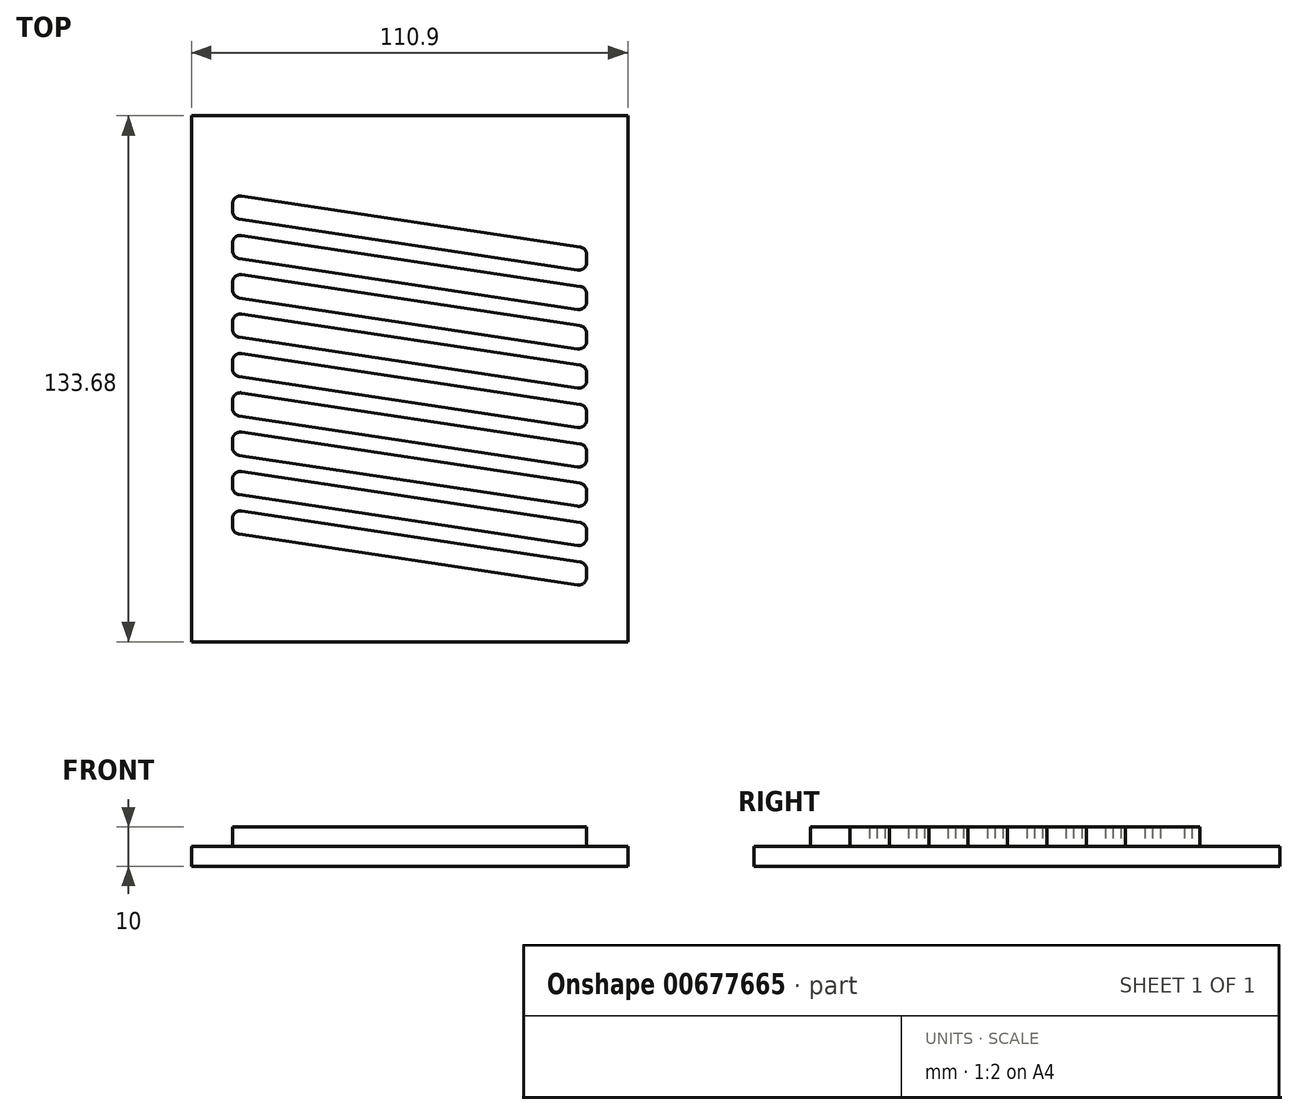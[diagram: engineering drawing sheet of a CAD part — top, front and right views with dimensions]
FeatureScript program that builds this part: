
annotation { "Feature Type Name" : "Feature", "Feature Type Description" : "" }
export const myFeature = defineFeature(function(context is Context, id is Id, definition is map)
    precondition{}
    {
        {
            var Q0;
            Q0=qCreatedBy(makeId("Top.planeOp"),FACE);
            var sketch = newSketch(context, id + "F0", { "sketchPlane" : qUnion([Q0])});
            skLineSegment(sketch, "E0.bottom", {"start": v(-45, -60) * mm, "end": v(45, -60) * mm});
            skLineSegment(sketch, "E0.left", {"start": v(-50, -55) * mm, "end": v(-50, 43.94) * mm});
            skLineSegment(sketch, "E0.right", {"start": v(50, -55) * mm, "end": v(50, 43.82) * mm});
            skPoint(sketch, "E0.middle", {"position": v(0, 0) * mm});
            skLineSegment(sketch, "E1.bottom", {"start": v(-40, -55) * mm, "end": v(10.03, -55) * mm});
            skLineSegment(sketch, "E1.right", {"start": v(45, -55) * mm, "end": v(45, -8.5) * mm, "construction": true});
            skLineSegment(sketch, "E2", {"start": v(-42.7, 6.43) * mm, "end": v(43.3, -6.51) * mm});
            skLineSegment(sketch, "E3", {"start": v(-43.3, 10.56) * mm, "end": v(42.7, -2.38) * mm});
            skLineSegment(sketch, "E4.trimOffspring", {"start": v(-45, 12.5) * mm, "end": v(-45, 12.82) * mm, "construction": true});
            skLineSegment(sketch, "E5.trimOffspring", {"start": v(45, -0.4) * mm, "end": v(45, 289.24) * mm, "construction": true});
            skPoint(sketch, "E6.visualSharp", {"position": v(-44.96, 10.8) * mm});
            skArc(sketch, "E6.filletArc", {"start": v(-45, 12.5) * mm, "mid": v(-44.5, 11.22) * mm, "end": v(-43.3, 10.56) * mm});
            skPoint(sketch, "E7.visualSharp", {"position": v(45, -2.73) * mm});
            skArc(sketch, "E7.filletArc", {"start": v(42.7, -2.38) * mm, "mid": v(44.3, -1.92) * mm, "end": v(45, -0.4) * mm});
            skPoint(sketch, "E8.visualSharp", {"position": v(45, -6.77) * mm});
            skArc(sketch, "E8.filletArc", {"start": v(45, -8.5) * mm, "mid": v(44.5, -7.19) * mm, "end": v(43.3, -6.51) * mm});
            skPoint(sketch, "E9.visualSharp", {"position": v(-45, 6.77) * mm});
            skArc(sketch, "E9.filletArc", {"start": v(-42.7, 6.43) * mm, "mid": v(-44.32, 5.95) * mm, "end": v(-45, 4.4) * mm});
            skLineSegment(sketch, "E10", {"start": v(-45, 1.54) * mm, "end": v(-45, 12.82) * mm, "construction": true});
            skLineSegment(sketch, "E11", {"start": v(45, -13.88) * mm, "end": v(45, 7.22) * mm, "construction": true});
            skLineSegment(sketch, "E12.0.1.0", {"start": v(-42.7, 16.43) * mm, "end": v(43.3, 3.49) * mm});
            skLineSegment(sketch, "E12.0.1.1", {"start": v(-43.3, 20.56) * mm, "end": v(42.7, 7.62) * mm});
            skArc(sketch, "E12.0.1.2", {"start": v(45, 1.5) * mm, "mid": v(44.5, 2.81) * mm, "end": v(43.3, 3.49) * mm});
            skArc(sketch, "E12.0.1.3", {"start": v(42.7, 7.62) * mm, "mid": v(44.3, 8.08) * mm, "end": v(45, 9.6) * mm});
            skArc(sketch, "E12.0.1.4", {"start": v(-42.7, 16.43) * mm, "mid": v(-44.32, 15.95) * mm, "end": v(-45, 14.4) * mm});
            skArc(sketch, "E12.0.1.5", {"start": v(-45, 22.5) * mm, "mid": v(-44.5, 21.22) * mm, "end": v(-43.3, 20.56) * mm});
            skLineSegment(sketch, "E12.0.2.0", {"start": v(-42.7, 26.43) * mm, "end": v(43.3, 13.49) * mm});
            skLineSegment(sketch, "E12.0.2.1", {"start": v(-43.3, 30.56) * mm, "end": v(42.7, 17.62) * mm});
            skArc(sketch, "E12.0.2.2", {"start": v(45, 11.5) * mm, "mid": v(44.5, 12.81) * mm, "end": v(43.3, 13.49) * mm});
            skArc(sketch, "E12.0.2.3", {"start": v(42.7, 17.62) * mm, "mid": v(44.3, 18.08) * mm, "end": v(45, 19.6) * mm});
            skArc(sketch, "E12.0.2.4", {"start": v(-42.7, 26.43) * mm, "mid": v(-44.32, 25.95) * mm, "end": v(-45, 24.4) * mm});
            skArc(sketch, "E12.0.2.5", {"start": v(-45, 32.5) * mm, "mid": v(-44.5, 31.22) * mm, "end": v(-43.3, 30.56) * mm});
            skLineSegment(sketch, "E12.0.3.0", {"start": v(-42.7, 36.43) * mm, "end": v(43.3, 23.49) * mm});
            skLineSegment(sketch, "E12.0.3.1", {"start": v(-43.3, 40.56) * mm, "end": v(42.7, 27.62) * mm});
            skArc(sketch, "E12.0.3.2", {"start": v(45, 21.5) * mm, "mid": v(44.5, 22.81) * mm, "end": v(43.3, 23.49) * mm});
            skArc(sketch, "E12.0.3.3", {"start": v(42.7, 27.62) * mm, "mid": v(44.3, 28.08) * mm, "end": v(45, 29.6) * mm});
            skArc(sketch, "E12.0.3.4", {"start": v(-42.7, 36.43) * mm, "mid": v(-44.32, 35.95) * mm, "end": v(-45, 34.4) * mm});
            skArc(sketch, "E12.0.3.5", {"start": v(-45, 42.5) * mm, "mid": v(-44.5, 41.22) * mm, "end": v(-43.3, 40.56) * mm});
            skLineSegment(sketch, "E12.0.4.0", {"start": v(-42.7, 46.43) * mm, "end": v(43.3, 33.49) * mm});
            skLineSegment(sketch, "E12.0.4.1", {"start": v(-16.92, 46.6) * mm, "end": v(42.7, 37.62) * mm});
            skArc(sketch, "E12.0.4.2", {"start": v(45, 31.5) * mm, "mid": v(44.5, 32.81) * mm, "end": v(43.3, 33.49) * mm});
            skArc(sketch, "E12.0.4.3", {"start": v(42.7, 37.62) * mm, "mid": v(44.3, 38.08) * mm, "end": v(45, 39.6) * mm});
            skArc(sketch, "E12.0.4.4", {"start": v(-42.7, 46.43) * mm, "mid": v(-44.32, 45.95) * mm, "end": v(-45, 44.4) * mm});
            skArc(sketch, "E12.0.5.2", {"start": v(45, 41.5) * mm, "mid": v(44.5, 42.81) * mm, "end": v(43.3, 43.49) * mm});
            skArc(sketch, "E12.0.5.4", {"start": v(-44.92, 55) * mm, "mid": v(-44.99, 54.7) * mm, "end": v(-45, 54.4) * mm});
            skLineSegment(sketch, "E12.1.0.0", {"start": v(-42.71, -3.57) * mm, "end": v(43.28, -16.51) * mm});
            skLineSegment(sketch, "E12.1.0.1", {"start": v(-43.3, 0.56) * mm, "end": v(42.69, -12.38) * mm});
            skArc(sketch, "E12.1.0.2", {"start": v(44.98, -18.5) * mm, "mid": v(44.5, -17.19) * mm, "end": v(43.28, -16.51) * mm});
            skArc(sketch, "E12.1.0.3", {"start": v(42.69, -12.38) * mm, "mid": v(44.29, -11.92) * mm, "end": v(44.98, -10.4) * mm});
            skArc(sketch, "E12.1.0.4", {"start": v(-42.71, -3.57) * mm, "mid": v(-44.33, -4.05) * mm, "end": v(-45.01, -5.6) * mm});
            skArc(sketch, "E12.1.0.5", {"start": v(-45, 2.5) * mm, "mid": v(-44.5, 1.22) * mm, "end": v(-43.3, 0.56) * mm});
            skLineSegment(sketch, "E12.1.1.0", {"start": v(-42.71, 6.43) * mm, "end": v(43.28, -6.51) * mm});
            skLineSegment(sketch, "E12.1.1.1", {"start": v(-43.3, 10.56) * mm, "end": v(42.69, -2.38) * mm});
            skArc(sketch, "E12.1.1.2", {"start": v(44.98, -8.5) * mm, "mid": v(44.5, -7.19) * mm, "end": v(43.28, -6.51) * mm});
            skArc(sketch, "E12.1.1.3", {"start": v(42.69, -2.38) * mm, "mid": v(44.29, -1.92) * mm, "end": v(44.98, -0.4) * mm});
            skArc(sketch, "E12.1.1.4", {"start": v(-42.71, 6.43) * mm, "mid": v(-44.33, 5.95) * mm, "end": v(-45.01, 4.4) * mm});
            skLineSegment(sketch, "E12.1.2.0", {"start": v(-42.71, 16.43) * mm, "end": v(43.28, 3.49) * mm});
            skLineSegment(sketch, "E12.1.2.1", {"start": v(-43.3, 20.56) * mm, "end": v(42.69, 7.62) * mm});
            skArc(sketch, "E12.1.2.2", {"start": v(44.98, 1.5) * mm, "mid": v(44.5, 2.81) * mm, "end": v(43.28, 3.49) * mm});
            skArc(sketch, "E12.1.2.3", {"start": v(42.69, 7.62) * mm, "mid": v(44.29, 8.08) * mm, "end": v(44.98, 9.6) * mm});
            skArc(sketch, "E12.1.2.4", {"start": v(-42.71, 16.43) * mm, "mid": v(-44.33, 15.95) * mm, "end": v(-45.01, 14.4) * mm});
            skArc(sketch, "E12.1.2.5", {"start": v(-45, 22.5) * mm, "mid": v(-44.5, 21.22) * mm, "end": v(-43.3, 20.56) * mm});
            skLineSegment(sketch, "E12.1.3.0", {"start": v(-42.71, 26.43) * mm, "end": v(43.28, 13.49) * mm});
            skLineSegment(sketch, "E12.1.3.1", {"start": v(-43.3, 30.56) * mm, "end": v(42.69, 17.62) * mm});
            skArc(sketch, "E12.1.3.2", {"start": v(44.98, 11.5) * mm, "mid": v(44.5, 12.81) * mm, "end": v(43.28, 13.49) * mm});
            skArc(sketch, "E12.1.3.3", {"start": v(42.69, 17.62) * mm, "mid": v(44.29, 18.08) * mm, "end": v(44.98, 19.6) * mm});
            skArc(sketch, "E12.1.3.4", {"start": v(-42.71, 26.43) * mm, "mid": v(-44.33, 25.95) * mm, "end": v(-45.01, 24.4) * mm});
            skArc(sketch, "E12.1.3.5", {"start": v(-45, 32.5) * mm, "mid": v(-44.5, 31.22) * mm, "end": v(-43.3, 30.56) * mm});
            skLineSegment(sketch, "E12.1.4.0", {"start": v(-42.71, 36.43) * mm, "end": v(43.28, 23.49) * mm});
            skLineSegment(sketch, "E12.1.4.1", {"start": v(-43.3, 40.56) * mm, "end": v(42.69, 27.62) * mm});
            skArc(sketch, "E12.1.4.2", {"start": v(44.98, 21.5) * mm, "mid": v(44.5, 22.81) * mm, "end": v(43.28, 23.49) * mm});
            skArc(sketch, "E12.1.4.3", {"start": v(42.69, 27.62) * mm, "mid": v(44.29, 28.08) * mm, "end": v(44.98, 29.6) * mm});
            skArc(sketch, "E12.1.4.4", {"start": v(-42.71, 36.43) * mm, "mid": v(-44.33, 35.95) * mm, "end": v(-45.01, 34.4) * mm});
            skArc(sketch, "E12.1.4.5", {"start": v(-45, 42.5) * mm, "mid": v(-44.5, 41.22) * mm, "end": v(-43.3, 40.56) * mm});
            skLineSegment(sketch, "E12.1.5.0", {"start": v(-42.71, 46.43) * mm, "end": v(43.28, 33.49) * mm});
            skArc(sketch, "E12.1.5.2", {"start": v(44.98, 31.5) * mm, "mid": v(44.5, 32.81) * mm, "end": v(43.28, 33.49) * mm});
            skArc(sketch, "E12.1.5.3", {"start": v(42.69, 37.62) * mm, "mid": v(44.29, 38.08) * mm, "end": v(44.98, 39.6) * mm});
            skArc(sketch, "E12.1.5.4", {"start": v(-42.71, 46.43) * mm, "mid": v(-44.33, 45.95) * mm, "end": v(-45.01, 44.4) * mm});
            skLineSegment(sketch, "E12.2.0.0", {"start": v(-42.72, -13.57) * mm, "end": v(43.27, -26.51) * mm});
            skLineSegment(sketch, "E12.2.0.1", {"start": v(-43.31, -9.44) * mm, "end": v(42.68, -22.38) * mm});
            skArc(sketch, "E12.2.0.2", {"start": v(44.97, -28.5) * mm, "mid": v(44.49, -27.19) * mm, "end": v(43.27, -26.51) * mm});
            skArc(sketch, "E12.2.0.3", {"start": v(42.68, -22.38) * mm, "mid": v(44.28, -21.92) * mm, "end": v(44.97, -20.4) * mm});
            skArc(sketch, "E12.2.0.4", {"start": v(-42.72, -13.57) * mm, "mid": v(-44.34, -14.05) * mm, "end": v(-45.02, -15.6) * mm});
            skArc(sketch, "E12.2.0.5", {"start": v(-45.01, -7.5) * mm, "mid": v(-44.51, -8.78) * mm, "end": v(-43.31, -9.44) * mm});
            skLineSegment(sketch, "E12.2.1.0", {"start": v(-42.72, -3.57) * mm, "end": v(43.27, -16.51) * mm});
            skLineSegment(sketch, "E12.2.1.1", {"start": v(-43.31, 0.56) * mm, "end": v(42.68, -12.38) * mm});
            skArc(sketch, "E12.2.1.2", {"start": v(44.97, -18.5) * mm, "mid": v(44.49, -17.19) * mm, "end": v(43.27, -16.51) * mm});
            skArc(sketch, "E12.2.1.3", {"start": v(42.68, -12.38) * mm, "mid": v(44.28, -11.92) * mm, "end": v(44.97, -10.4) * mm});
            skArc(sketch, "E12.2.1.4", {"start": v(-42.72, -3.57) * mm, "mid": v(-44.34, -4.05) * mm, "end": v(-45.02, -5.6) * mm});
            skArc(sketch, "E12.2.1.5", {"start": v(-45.01, 2.5) * mm, "mid": v(-44.51, 1.22) * mm, "end": v(-43.31, 0.56) * mm});
            skLineSegment(sketch, "E12.2.2.0", {"start": v(-42.72, 6.43) * mm, "end": v(43.27, -6.51) * mm});
            skLineSegment(sketch, "E12.2.2.1", {"start": v(-43.31, 10.56) * mm, "end": v(42.68, -2.38) * mm});
            skArc(sketch, "E12.2.2.2", {"start": v(44.97, -8.5) * mm, "mid": v(44.49, -7.19) * mm, "end": v(43.27, -6.51) * mm});
            skArc(sketch, "E12.2.2.3", {"start": v(42.68, -2.38) * mm, "mid": v(44.28, -1.92) * mm, "end": v(44.97, -0.4) * mm});
            skArc(sketch, "E12.2.2.4", {"start": v(-42.72, 6.43) * mm, "mid": v(-44.34, 5.95) * mm, "end": v(-45.02, 4.4) * mm});
            skArc(sketch, "E12.2.2.5", {"start": v(-45.01, 12.5) * mm, "mid": v(-44.51, 11.22) * mm, "end": v(-43.31, 10.56) * mm});
            skLineSegment(sketch, "E12.2.3.0", {"start": v(-42.72, 16.43) * mm, "end": v(43.27, 3.49) * mm});
            skLineSegment(sketch, "E12.2.3.1", {"start": v(-43.31, 20.56) * mm, "end": v(42.68, 7.62) * mm});
            skArc(sketch, "E12.2.3.2", {"start": v(44.97, 1.5) * mm, "mid": v(44.49, 2.81) * mm, "end": v(43.27, 3.49) * mm});
            skArc(sketch, "E12.2.3.3", {"start": v(42.68, 7.62) * mm, "mid": v(44.28, 8.08) * mm, "end": v(44.97, 9.6) * mm});
            skArc(sketch, "E12.2.3.4", {"start": v(-42.72, 16.43) * mm, "mid": v(-44.34, 15.95) * mm, "end": v(-45.02, 14.4) * mm});
            skArc(sketch, "E12.2.3.5", {"start": v(-45.01, 22.5) * mm, "mid": v(-44.51, 21.22) * mm, "end": v(-43.31, 20.56) * mm});
            skLineSegment(sketch, "E12.2.4.0", {"start": v(-42.72, 26.43) * mm, "end": v(43.27, 13.49) * mm});
            skLineSegment(sketch, "E12.2.4.1", {"start": v(-43.31, 30.56) * mm, "end": v(42.68, 17.62) * mm});
            skArc(sketch, "E12.2.4.2", {"start": v(44.97, 11.5) * mm, "mid": v(44.49, 12.81) * mm, "end": v(43.27, 13.49) * mm});
            skArc(sketch, "E12.2.4.3", {"start": v(42.68, 17.62) * mm, "mid": v(44.28, 18.08) * mm, "end": v(44.97, 19.6) * mm});
            skArc(sketch, "E12.2.4.4", {"start": v(-42.72, 26.43) * mm, "mid": v(-44.34, 25.95) * mm, "end": v(-45.02, 24.4) * mm});
            skArc(sketch, "E12.2.4.5", {"start": v(-45.01, 32.5) * mm, "mid": v(-44.51, 31.22) * mm, "end": v(-43.31, 30.56) * mm});
            skLineSegment(sketch, "E12.2.5.0", {"start": v(-42.72, 36.43) * mm, "end": v(43.27, 23.49) * mm});
            skLineSegment(sketch, "E12.2.5.1", {"start": v(-43.31, 40.56) * mm, "end": v(42.68, 27.62) * mm});
            skArc(sketch, "E12.2.5.2", {"start": v(44.97, 21.5) * mm, "mid": v(44.49, 22.81) * mm, "end": v(43.27, 23.49) * mm});
            skArc(sketch, "E12.2.5.3", {"start": v(42.68, 27.62) * mm, "mid": v(44.28, 28.08) * mm, "end": v(44.97, 29.6) * mm});
            skArc(sketch, "E12.2.5.4", {"start": v(-42.72, 36.43) * mm, "mid": v(-44.34, 35.95) * mm, "end": v(-45.02, 34.4) * mm});
            skArc(sketch, "E12.2.5.5", {"start": v(-45.01, 42.5) * mm, "mid": v(-44.51, 41.22) * mm, "end": v(-43.31, 40.56) * mm});
            skLineSegment(sketch, "E12.3.0.0", {"start": v(-42.73, -23.57) * mm, "end": v(43.26, -36.51) * mm});
            skLineSegment(sketch, "E12.3.0.1", {"start": v(-43.32, -19.44) * mm, "end": v(42.67, -32.38) * mm});
            skArc(sketch, "E12.3.0.2", {"start": v(44.96, -38.5) * mm, "mid": v(44.48, -37.19) * mm, "end": v(43.26, -36.51) * mm});
            skArc(sketch, "E12.3.0.3", {"start": v(42.67, -32.38) * mm, "mid": v(44.27, -31.92) * mm, "end": v(44.96, -30.4) * mm});
            skArc(sketch, "E12.3.0.4", {"start": v(-42.73, -23.57) * mm, "mid": v(-44.35, -24.05) * mm, "end": v(-45.03, -25.6) * mm});
            skArc(sketch, "E12.3.0.5", {"start": v(-45.02, -17.5) * mm, "mid": v(-44.52, -18.78) * mm, "end": v(-43.32, -19.44) * mm});
            skLineSegment(sketch, "E12.3.1.0", {"start": v(-42.73, -13.57) * mm, "end": v(43.26, -26.51) * mm});
            skLineSegment(sketch, "E12.3.1.1", {"start": v(-43.32, -9.44) * mm, "end": v(42.67, -22.38) * mm});
            skArc(sketch, "E12.3.1.2", {"start": v(44.96, -28.5) * mm, "mid": v(44.48, -27.19) * mm, "end": v(43.26, -26.51) * mm});
            skArc(sketch, "E12.3.1.3", {"start": v(42.67, -22.38) * mm, "mid": v(44.27, -21.92) * mm, "end": v(44.96, -20.4) * mm});
            skArc(sketch, "E12.3.1.4", {"start": v(-42.73, -13.57) * mm, "mid": v(-44.35, -14.05) * mm, "end": v(-45.03, -15.6) * mm});
            skArc(sketch, "E12.3.1.5", {"start": v(-45.02, -7.5) * mm, "mid": v(-44.52, -8.78) * mm, "end": v(-43.32, -9.44) * mm});
            skLineSegment(sketch, "E12.3.2.0", {"start": v(-42.73, -3.57) * mm, "end": v(43.26, -16.51) * mm});
            skLineSegment(sketch, "E12.3.2.1", {"start": v(-43.32, 0.56) * mm, "end": v(42.67, -12.38) * mm});
            skArc(sketch, "E12.3.2.2", {"start": v(44.96, -18.5) * mm, "mid": v(44.48, -17.19) * mm, "end": v(43.26, -16.51) * mm});
            skArc(sketch, "E12.3.2.3", {"start": v(42.67, -12.38) * mm, "mid": v(44.27, -11.92) * mm, "end": v(44.96, -10.4) * mm});
            skArc(sketch, "E12.3.2.4", {"start": v(-42.73, -3.57) * mm, "mid": v(-44.35, -4.05) * mm, "end": v(-45.03, -5.6) * mm});
            skArc(sketch, "E12.3.2.5", {"start": v(-45.02, 2.5) * mm, "mid": v(-44.52, 1.22) * mm, "end": v(-43.32, 0.56) * mm});
            skLineSegment(sketch, "E12.3.3.0", {"start": v(-42.73, 6.43) * mm, "end": v(43.26, -6.51) * mm});
            skLineSegment(sketch, "E12.3.3.1", {"start": v(-43.32, 10.56) * mm, "end": v(42.67, -2.38) * mm});
            skArc(sketch, "E12.3.3.2", {"start": v(44.96, -8.5) * mm, "mid": v(44.48, -7.19) * mm, "end": v(43.26, -6.51) * mm});
            skArc(sketch, "E12.3.3.3", {"start": v(42.67, -2.38) * mm, "mid": v(44.27, -1.92) * mm, "end": v(44.96, -0.4) * mm});
            skArc(sketch, "E12.3.3.4", {"start": v(-42.73, 6.43) * mm, "mid": v(-44.35, 5.95) * mm, "end": v(-45.03, 4.4) * mm});
            skArc(sketch, "E12.3.3.5", {"start": v(-45.02, 12.5) * mm, "mid": v(-44.52, 11.22) * mm, "end": v(-43.32, 10.56) * mm});
            skLineSegment(sketch, "E12.3.4.0", {"start": v(-42.73, 16.43) * mm, "end": v(43.26, 3.49) * mm});
            skLineSegment(sketch, "E12.3.4.1", {"start": v(-43.32, 20.56) * mm, "end": v(42.67, 7.62) * mm});
            skArc(sketch, "E12.3.4.2", {"start": v(44.96, 1.5) * mm, "mid": v(44.48, 2.81) * mm, "end": v(43.26, 3.49) * mm});
            skArc(sketch, "E12.3.4.3", {"start": v(42.67, 7.62) * mm, "mid": v(44.27, 8.08) * mm, "end": v(44.96, 9.6) * mm});
            skArc(sketch, "E12.3.4.4", {"start": v(-42.73, 16.43) * mm, "mid": v(-44.35, 15.95) * mm, "end": v(-45.03, 14.4) * mm});
            skArc(sketch, "E12.3.4.5", {"start": v(-45.02, 22.5) * mm, "mid": v(-44.52, 21.22) * mm, "end": v(-43.32, 20.56) * mm});
            skLineSegment(sketch, "E12.3.5.0", {"start": v(-42.73, 26.43) * mm, "end": v(43.26, 13.49) * mm});
            skLineSegment(sketch, "E12.3.5.1", {"start": v(-43.32, 30.56) * mm, "end": v(42.67, 17.62) * mm});
            skArc(sketch, "E12.3.5.2", {"start": v(44.96, 11.5) * mm, "mid": v(44.48, 12.81) * mm, "end": v(43.26, 13.49) * mm});
            skArc(sketch, "E12.3.5.3", {"start": v(42.67, 17.62) * mm, "mid": v(44.27, 18.08) * mm, "end": v(44.96, 19.6) * mm});
            skArc(sketch, "E12.3.5.4", {"start": v(-42.73, 26.43) * mm, "mid": v(-44.35, 25.95) * mm, "end": v(-45.03, 24.4) * mm});
            skArc(sketch, "E12.3.5.5", {"start": v(-45.02, 32.5) * mm, "mid": v(-44.52, 31.22) * mm, "end": v(-43.32, 30.56) * mm});
            skLineSegment(sketch, "E12.4.0.0", {"start": v(-42.74, -33.57) * mm, "end": v(43.25, -46.51) * mm});
            skLineSegment(sketch, "E12.4.0.1", {"start": v(-43.33, -29.44) * mm, "end": v(42.66, -42.38) * mm});
            skArc(sketch, "E12.4.0.2", {"start": v(44.95, -48.5) * mm, "mid": v(44.47, -47.19) * mm, "end": v(43.25, -46.51) * mm});
            skArc(sketch, "E12.4.0.3", {"start": v(42.66, -42.38) * mm, "mid": v(44.26, -41.92) * mm, "end": v(44.95, -40.4) * mm});
            skArc(sketch, "E12.4.0.4", {"start": v(-42.74, -33.57) * mm, "mid": v(-44.36, -34.05) * mm, "end": v(-45.04, -35.6) * mm});
            skArc(sketch, "E12.4.0.5", {"start": v(-45.03, -27.5) * mm, "mid": v(-44.53, -28.78) * mm, "end": v(-43.33, -29.44) * mm});
            skLineSegment(sketch, "E12.4.1.0", {"start": v(-42.74, -23.57) * mm, "end": v(43.25, -36.51) * mm});
            skLineSegment(sketch, "E12.4.1.1", {"start": v(-43.33, -19.44) * mm, "end": v(42.66, -32.38) * mm});
            skArc(sketch, "E12.4.1.2", {"start": v(44.95, -38.5) * mm, "mid": v(44.47, -37.19) * mm, "end": v(43.25, -36.51) * mm});
            skArc(sketch, "E12.4.1.3", {"start": v(42.66, -32.38) * mm, "mid": v(44.26, -31.92) * mm, "end": v(44.95, -30.4) * mm});
            skArc(sketch, "E12.4.1.4", {"start": v(-42.74, -23.57) * mm, "mid": v(-44.36, -24.05) * mm, "end": v(-45.04, -25.6) * mm});
            skArc(sketch, "E12.4.1.5", {"start": v(-45.03, -17.5) * mm, "mid": v(-44.53, -18.78) * mm, "end": v(-43.33, -19.44) * mm});
            skLineSegment(sketch, "E12.4.2.0", {"start": v(-42.74, -13.57) * mm, "end": v(43.25, -26.51) * mm});
            skLineSegment(sketch, "E12.4.2.1", {"start": v(-43.33, -9.44) * mm, "end": v(42.66, -22.38) * mm});
            skArc(sketch, "E12.4.2.2", {"start": v(44.95, -28.5) * mm, "mid": v(44.47, -27.19) * mm, "end": v(43.25, -26.51) * mm});
            skArc(sketch, "E12.4.2.3", {"start": v(42.66, -22.38) * mm, "mid": v(44.26, -21.92) * mm, "end": v(44.95, -20.4) * mm});
            skArc(sketch, "E12.4.2.4", {"start": v(-42.74, -13.57) * mm, "mid": v(-44.36, -14.05) * mm, "end": v(-45.04, -15.6) * mm});
            skArc(sketch, "E12.4.2.5", {"start": v(-45.03, -7.5) * mm, "mid": v(-44.53, -8.78) * mm, "end": v(-43.33, -9.44) * mm});
            skLineSegment(sketch, "E12.4.3.0", {"start": v(-42.74, -3.57) * mm, "end": v(43.25, -16.51) * mm});
            skLineSegment(sketch, "E12.4.3.1", {"start": v(-43.33, 0.56) * mm, "end": v(42.66, -12.38) * mm});
            skArc(sketch, "E12.4.3.2", {"start": v(44.95, -18.5) * mm, "mid": v(44.47, -17.19) * mm, "end": v(43.25, -16.51) * mm});
            skArc(sketch, "E12.4.3.3", {"start": v(42.66, -12.38) * mm, "mid": v(44.26, -11.92) * mm, "end": v(44.95, -10.4) * mm});
            skArc(sketch, "E12.4.3.4", {"start": v(-42.74, -3.57) * mm, "mid": v(-44.36, -4.05) * mm, "end": v(-45.04, -5.6) * mm});
            skArc(sketch, "E12.4.3.5", {"start": v(-45.03, 2.5) * mm, "mid": v(-44.53, 1.22) * mm, "end": v(-43.33, 0.56) * mm});
            skLineSegment(sketch, "E12.4.4.0", {"start": v(-42.74, 6.43) * mm, "end": v(43.25, -6.51) * mm});
            skLineSegment(sketch, "E12.4.4.1", {"start": v(-43.33, 10.56) * mm, "end": v(42.66, -2.38) * mm});
            skArc(sketch, "E12.4.4.2", {"start": v(44.95, -8.5) * mm, "mid": v(44.47, -7.19) * mm, "end": v(43.25, -6.51) * mm});
            skArc(sketch, "E12.4.4.3", {"start": v(42.66, -2.38) * mm, "mid": v(44.26, -1.92) * mm, "end": v(44.95, -0.4) * mm});
            skArc(sketch, "E12.4.4.4", {"start": v(-42.74, 6.43) * mm, "mid": v(-44.36, 5.95) * mm, "end": v(-45.04, 4.4) * mm});
            skArc(sketch, "E12.4.4.5", {"start": v(-45.03, 12.5) * mm, "mid": v(-44.53, 11.22) * mm, "end": v(-43.33, 10.56) * mm});
            skLineSegment(sketch, "E12.4.5.0", {"start": v(-42.74, 16.43) * mm, "end": v(43.25, 3.49) * mm});
            skLineSegment(sketch, "E12.4.5.1", {"start": v(-43.33, 20.56) * mm, "end": v(42.66, 7.62) * mm});
            skArc(sketch, "E12.4.5.2", {"start": v(44.95, 1.5) * mm, "mid": v(44.47, 2.81) * mm, "end": v(43.25, 3.49) * mm});
            skArc(sketch, "E12.4.5.3", {"start": v(42.66, 7.62) * mm, "mid": v(44.26, 8.08) * mm, "end": v(44.95, 9.6) * mm});
            skArc(sketch, "E12.4.5.4", {"start": v(-42.74, 16.43) * mm, "mid": v(-44.36, 15.95) * mm, "end": v(-45.04, 14.4) * mm});
            skArc(sketch, "E12.4.5.5", {"start": v(-45.03, 22.5) * mm, "mid": v(-44.53, 21.22) * mm, "end": v(-43.33, 20.56) * mm});
            skLineSegment(sketch, "E12.5.0.0", {"start": v(-42.75, -43.57) * mm, "end": v(-7.57, -48.87) * mm});
            skLineSegment(sketch, "E12.5.0.1", {"start": v(-43.34, -39.44) * mm, "end": v(42.65, -52.38) * mm});
            skArc(sketch, "E12.5.0.3", {"start": v(42.65, -52.38) * mm, "mid": v(44.25, -51.92) * mm, "end": v(44.94, -50.4) * mm});
            skArc(sketch, "E12.5.0.4", {"start": v(-42.75, -43.57) * mm, "mid": v(-44.37, -44.05) * mm, "end": v(-45.05, -45.6) * mm});
            skArc(sketch, "E12.5.0.5", {"start": v(-45.04, -37.5) * mm, "mid": v(-44.54, -38.78) * mm, "end": v(-43.34, -39.44) * mm});
            skLineSegment(sketch, "E12.5.1.0", {"start": v(-42.75, -33.57) * mm, "end": v(43.24, -46.51) * mm});
            skLineSegment(sketch, "E12.5.1.1", {"start": v(-43.34, -29.44) * mm, "end": v(42.65, -42.38) * mm});
            skArc(sketch, "E12.5.1.2", {"start": v(44.94, -48.5) * mm, "mid": v(44.46, -47.19) * mm, "end": v(43.24, -46.51) * mm});
            skArc(sketch, "E12.5.1.3", {"start": v(42.65, -42.38) * mm, "mid": v(44.25, -41.92) * mm, "end": v(44.94, -40.4) * mm});
            skArc(sketch, "E12.5.1.4", {"start": v(-42.75, -33.57) * mm, "mid": v(-44.37, -34.05) * mm, "end": v(-45.05, -35.6) * mm});
            skArc(sketch, "E12.5.1.5", {"start": v(-45.04, -27.5) * mm, "mid": v(-44.54, -28.78) * mm, "end": v(-43.34, -29.44) * mm});
            skLineSegment(sketch, "E12.5.2.0", {"start": v(-42.75, -23.57) * mm, "end": v(43.24, -36.51) * mm});
            skLineSegment(sketch, "E12.5.2.1", {"start": v(-43.34, -19.44) * mm, "end": v(42.65, -32.38) * mm});
            skArc(sketch, "E12.5.2.2", {"start": v(44.94, -38.5) * mm, "mid": v(44.46, -37.19) * mm, "end": v(43.24, -36.51) * mm});
            skArc(sketch, "E12.5.2.3", {"start": v(42.65, -32.38) * mm, "mid": v(44.25, -31.92) * mm, "end": v(44.94, -30.4) * mm});
            skArc(sketch, "E12.5.2.4", {"start": v(-42.75, -23.57) * mm, "mid": v(-44.37, -24.05) * mm, "end": v(-45.05, -25.6) * mm});
            skArc(sketch, "E12.5.2.5", {"start": v(-45.04, -17.5) * mm, "mid": v(-44.54, -18.78) * mm, "end": v(-43.34, -19.44) * mm});
            skLineSegment(sketch, "E12.5.3.0", {"start": v(-42.75, -13.57) * mm, "end": v(43.24, -26.51) * mm});
            skLineSegment(sketch, "E12.5.3.1", {"start": v(-43.34, -9.44) * mm, "end": v(42.65, -22.38) * mm});
            skArc(sketch, "E12.5.3.2", {"start": v(44.94, -28.5) * mm, "mid": v(44.46, -27.19) * mm, "end": v(43.24, -26.51) * mm});
            skArc(sketch, "E12.5.3.3", {"start": v(42.65, -22.38) * mm, "mid": v(44.25, -21.92) * mm, "end": v(44.94, -20.4) * mm});
            skArc(sketch, "E12.5.3.4", {"start": v(-42.75, -13.57) * mm, "mid": v(-44.37, -14.05) * mm, "end": v(-45.05, -15.6) * mm});
            skArc(sketch, "E12.5.3.5", {"start": v(-45.04, -7.5) * mm, "mid": v(-44.54, -8.78) * mm, "end": v(-43.34, -9.44) * mm});
            skLineSegment(sketch, "E12.5.4.0", {"start": v(-42.75, -3.57) * mm, "end": v(43.24, -16.51) * mm});
            skLineSegment(sketch, "E12.5.4.1", {"start": v(-43.34, 0.56) * mm, "end": v(42.65, -12.38) * mm});
            skArc(sketch, "E12.5.4.2", {"start": v(44.94, -18.5) * mm, "mid": v(44.46, -17.19) * mm, "end": v(43.24, -16.51) * mm});
            skArc(sketch, "E12.5.4.3", {"start": v(42.65, -12.38) * mm, "mid": v(44.25, -11.92) * mm, "end": v(44.94, -10.4) * mm});
            skArc(sketch, "E12.5.4.4", {"start": v(-42.75, -3.57) * mm, "mid": v(-44.37, -4.05) * mm, "end": v(-45.05, -5.6) * mm});
            skArc(sketch, "E12.5.4.5", {"start": v(-45.04, 2.5) * mm, "mid": v(-44.54, 1.22) * mm, "end": v(-43.34, 0.56) * mm});
            skLineSegment(sketch, "E12.5.5.0", {"start": v(-42.75, 6.43) * mm, "end": v(43.24, -6.51) * mm});
            skLineSegment(sketch, "E12.5.5.1", {"start": v(-43.34, 10.56) * mm, "end": v(42.65, -2.38) * mm});
            skArc(sketch, "E12.5.5.2", {"start": v(44.94, -8.5) * mm, "mid": v(44.46, -7.19) * mm, "end": v(43.24, -6.51) * mm});
            skArc(sketch, "E12.5.5.3", {"start": v(42.65, -2.38) * mm, "mid": v(44.25, -1.92) * mm, "end": v(44.94, -0.4) * mm});
            skArc(sketch, "E12.5.5.4", {"start": v(-42.75, 6.43) * mm, "mid": v(-44.37, 5.95) * mm, "end": v(-45.05, 4.4) * mm});
            skArc(sketch, "E12.5.5.5", {"start": v(-45.04, 12.5) * mm, "mid": v(-44.54, 11.22) * mm, "end": v(-43.34, 10.56) * mm});
            skLineSegment(sketch, "E12.direction1", {"start": v(-42.7, 6.43) * mm, "end": v(-42.71, -3.57) * mm, "construction": true});
            skLineSegment(sketch, "E12.direction2", {"start": v(-42.7, 6.43) * mm, "end": v(-42.7, 16.43) * mm, "construction": true});
            skPoint(sketch, "E13.orphan", {"position": v(-42.7, 56.43) * mm});
            skPoint(sketch, "E14.visualSharp", {"position": v(45, 55) * mm});
            skPoint(sketch, "E15.visualSharp", {"position": v(50, 60) * mm});
            skPoint(sketch, "E16.visualSharp", {"position": v(-50, 60) * mm});
            skPoint(sketch, "E17.visualSharp", {"position": v(50, -60) * mm});
            skArc(sketch, "E17.filletArc", {"start": v(45, -60) * mm, "mid": v(48.54, -58.54) * mm, "end": v(50, -55) * mm});
            skPoint(sketch, "E18.visualSharp", {"position": v(-45, -55) * mm});
            skArc(sketch, "E18.filletArc", {"start": v(-45, -50) * mm, "mid": v(-43.54, -53.54) * mm, "end": v(-40, -55) * mm});
            skPoint(sketch, "E19.visualSharp", {"position": v(-50, -60) * mm});
            skArc(sketch, "E19.filletArc", {"start": v(-50, -55) * mm, "mid": v(-48.54, -58.54) * mm, "end": v(-45, -60) * mm});
            skLineSegment(sketch, "E20", {"start": v(-6.98, 65.52) * mm, "end": v(-5, 65.52) * mm});
            skLineSegment(sketch, "E21", {"start": v(-5, 65.52) * mm, "end": v(-5, 62.51) * mm});
            skLineSegment(sketch, "E22", {"start": v(-5, 62.51) * mm, "end": v(5, 62.51) * mm});
            skLineSegment(sketch, "E23", {"start": v(5, 62.51) * mm, "end": v(5, 65.52) * mm});
            skLineSegment(sketch, "E24", {"start": v(-43.5, 51.8) * mm, "end": v(-16.56, 56.91) * mm});
            skLineSegment(sketch, "E25", {"start": v(43.4, 51.7) * mm, "end": v(18.5, 56.14) * mm});
            skArc(sketch, "E26.trimOffspring", {"start": v(-43.3, 50.52) * mm, "mid": v(-43.3, 50.54) * mm, "end": v(-43.3, 50.56) * mm});
            skPoint(sketch, "E27.orphan", {"position": v(-45, 52.5) * mm});
            skLineSegment(sketch, "E28.trimOffspring", {"start": v(-16.04, 52.41) * mm, "end": v(43.3, 43.49) * mm});
            skPoint(sketch, "E29.endSnap0", {"position": v(44.5, 42.81) * mm});
            skPoint(sketch, "E30.visualSharp", {"position": v(-18.02, 52.71) * mm});
            skLineSegment(sketch, "E31", {"start": v(-18.32, 50.73) * mm, "end": v(-18.6, 48.87) * mm});
            skArc(sketch, "E32.filletArc", {"start": v(-16.04, 52.41) * mm, "mid": v(-17.53, 52.04) * mm, "end": v(-18.32, 50.73) * mm});
            skPoint(sketch, "E33.newPointB", {"position": v(-43.3, 50.56) * mm});
            skArc(sketch, "E33.filletArc", {"start": v(-18.6, 48.87) * mm, "mid": v(-18.23, 47.38) * mm, "end": v(-16.92, 46.6) * mm});
            skLineSegment(sketch, "E34.trimOffspring", {"start": v(5, 65.52) * mm, "end": v(6.98, 65.52) * mm});
            skLineSegment(sketch, "E35", {"start": v(-13, 60.9) * mm, "end": v(-13, 65.52) * mm});
            skLineSegment(sketch, "E36", {"start": v(-13, 65.52) * mm, "end": v(-6.98, 65.52) * mm});
            skLineSegment(sketch, "E37", {"start": v(13, 61.09) * mm, "end": v(13, 65.52) * mm});
            skLineSegment(sketch, "E38", {"start": v(13, 65.52) * mm, "end": v(6.98, 65.52) * mm});
            skPoint(sketch, "E39.visualSharp", {"position": v(-13, 57.59) * mm});
            skPoint(sketch, "E40.visualSharp", {"position": v(13, 57.12) * mm});
            skLineSegment(sketch, "E41", {"start": v(-5, 65.52) * mm, "end": v(-5, 58.52) * mm});
            skPoint(sketch, "E42.visualSharp", {"position": v(-50, 50.56) * mm});
            skArc(sketch, "E42.filletArc", {"start": v(-43.5, 51.8) * mm, "mid": v(-48.16, 49.04) * mm, "end": v(-50, 43.94) * mm});
            skPoint(sketch, "E43.visualSharp", {"position": v(50, 50.51) * mm});
            skArc(sketch, "E43.filletArc", {"start": v(50, 43.82) * mm, "mid": v(48.13, 48.95) * mm, "end": v(43.4, 51.7) * mm});
            skLineSegment(sketch, "E44", {"start": v(-45, 44.4) * mm, "end": v(-45, 42.5) * mm});
            skLineSegment(sketch, "E45", {"start": v(-45, 34.4) * mm, "end": v(-45, 32.5) * mm});
            skLineSegment(sketch, "E46", {"start": v(-45, 24.4) * mm, "end": v(-45, 22.5) * mm});
            skLineSegment(sketch, "E47", {"start": v(-45, 14.4) * mm, "end": v(-45, 12.5) * mm});
            skLineSegment(sketch, "E48", {"start": v(-45, 4.4) * mm, "end": v(-45, 2.5) * mm});
            skLineSegment(sketch, "E49", {"start": v(-45.02, -15.6) * mm, "end": v(-45.02, -17.5) * mm});
            skLineSegment(sketch, "E50", {"start": v(-45.03, -25.6) * mm, "end": v(-45.03, -27.5) * mm});
            skLineSegment(sketch, "E51", {"start": v(-45.04, -35.6) * mm, "end": v(-45.04, -37.5) * mm});
            skLineSegment(sketch, "E52", {"start": v(44.94, -50.4) * mm, "end": v(44.95, -48.5) * mm});
            skLineSegment(sketch, "E53", {"start": v(44.95, -40.4) * mm, "end": v(44.96, -38.5) * mm});
            skLineSegment(sketch, "E54", {"start": v(44.96, -30.4) * mm, "end": v(44.97, -28.5) * mm});
            skLineSegment(sketch, "E55", {"start": v(45, -0.4) * mm, "end": v(45, 1.5) * mm});
            skLineSegment(sketch, "E56", {"start": v(44.98, -10.4) * mm, "end": v(45, -8.5) * mm});
            skLineSegment(sketch, "E57", {"start": v(45, 11.5) * mm, "end": v(45, 9.6) * mm});
            skLineSegment(sketch, "E58", {"start": v(45, 19.6) * mm, "end": v(45, 21.5) * mm});
            skLineSegment(sketch, "E59", {"start": v(45, 29.6) * mm, "end": v(45, 31.5) * mm});
            skLineSegment(sketch, "E60", {"start": v(45, 39.6) * mm, "end": v(45, 41.5) * mm});
            skLineSegment(sketch, "E61", {"start": v(-45, -49.24) * mm, "end": v(-45.05, -45.6) * mm});
            skLineSegment(sketch, "E62", {"start": v(-45, -50) * mm, "end": v(-45, -49.24) * mm});
            skPoint(sketch, "E63.newPointB", {"position": v(-5.6, -49.24) * mm});
            skPoint(sketch, "E64.visualSharp", {"position": v(-6.46, -55) * mm});
            skLineSegment(sketch, "E65", {"start": v(-45.01, -5.6) * mm, "end": v(-45.01, -7.5) * mm});
            skLineSegment(sketch, "E66", {"start": v(44.98, -18.5) * mm, "end": v(44.97, -20.4) * mm});
            skLineSegment(sketch, "E67", {"start": v(-7.57, -48.87) * mm, "end": v(10.17, -51.54) * mm});
            skLineSegment(sketch, "E68", {"start": v(11.03, -52.53) * mm, "end": v(11.03, -54) * mm});
            skPoint(sketch, "E69.visualSharp", {"position": v(11.03, -51.67) * mm});
            skArc(sketch, "E69.filletArc", {"start": v(11.03, -52.53) * mm, "mid": v(10.78, -51.88) * mm, "end": v(10.17, -51.54) * mm});
            skPoint(sketch, "E70.visualSharp", {"position": v(11.03, -55) * mm});
            skArc(sketch, "E70.filletArc", {"start": v(10.03, -55) * mm, "mid": v(10.73, -54.7) * mm, "end": v(11.03, -54) * mm});
            skLineSegment(sketch, "E71", {"start": v(-6.98, 65.52) * mm, "end": v(-13.9, 58.35) * mm});
            skLineSegment(sketch, "E72", {"start": v(6.98, 65.52) * mm, "end": v(16.02, 57.35) * mm});
            skPoint(sketch, "E73.visualSharp", {"position": v(-15, 57.2) * mm});
            skArc(sketch, "E73.filletArc", {"start": v(-16.56, 56.91) * mm, "mid": v(-15.12, 57.42) * mm, "end": v(-13.9, 58.35) * mm});
            skPoint(sketch, "E74.visualSharp", {"position": v(17.08, 56.39) * mm});
            skArc(sketch, "E74.filletArc", {"start": v(16.02, 57.35) * mm, "mid": v(17.17, 56.57) * mm, "end": v(18.5, 56.14) * mm});
            skLineSegment(sketch, "E75.bottom", {"start": v(-57.5, -70) * mm, "end": v(57.5, -70) * mm});
            skLineSegment(sketch, "E75.top", {"start": v(-57.5, 70) * mm, "end": v(57.5, 70) * mm});
            skLineSegment(sketch, "E75.left", {"start": v(-57.5, -70) * mm, "end": v(-57.5, 70) * mm});
            skLineSegment(sketch, "E75.right", {"start": v(57.5, -70) * mm, "end": v(57.5, 70) * mm});
            skSolve(sketch);
        }
        {
            var Q0;
            {var subQ9=sQuery(id+"F0.wireOp",EDGE,"E12.1.0.0");Q0=makeQuery(id+"F0.imprint","IMPRINT",FACE,{"disambiguationData":[TD([[makeQuery(id+"F0.imprint","IMPRINT",EDGE,{"derivedFrom":subQ9}),-1.0]])]});}
            var Q1;
            {var subQ9=sQuery(id+"F0.wireOp",EDGE,"E12.2.0.0");Q1=makeQuery(id+"F0.imprint","IMPRINT",FACE,{"disambiguationData":[TD([[makeQuery(id+"F0.imprint","IMPRINT",EDGE,{"derivedFrom":subQ9}),-1.0]])]});}
            var Q2;
            {var subQ7=sQuery(id+"F0.wireOp",EDGE,"E12.3.0.0");Q2=makeQuery(id+"F0.imprint","IMPRINT",FACE,{"disambiguationData":[TD([[makeQuery(id+"F0.imprint","IMPRINT",EDGE,{"derivedFrom":subQ7}),-1.0]])]});}
            var Q3;
            {var subQ3=sQuery(id+"F0.wireOp",EDGE,"E12.4.0.0");Q3=makeQuery(id+"F0.imprint","IMPRINT",FACE,{"disambiguationData":[TD([[makeQuery(id+"F0.imprint","IMPRINT",EDGE,{"derivedFrom":subQ3}),-1.0]])]});}
            var Q4;
            {var subQ9=sQuery(id+"F0.wireOp",EDGE,"E2");Q4=makeQuery(id+"F0.imprint","IMPRINT",FACE,{"disambiguationData":[TD([[makeQuery(id+"F0.imprint","IMPRINT",EDGE,{"derivedFrom":subQ9}),-1.0]])]});}
            var Q5;
            {var subQ10=sQuery(id+"F0.wireOp",EDGE,"E3");Q5=makeQuery(id+"F0.imprint","IMPRINT",FACE,{"disambiguationData":[TD([[makeQuery(id+"F0.imprint","IMPRINT",EDGE,{"derivedFrom":subQ10}),1.0]])]});}
            var Q6;
            {var subQ7=sQuery(id+"F0.wireOp",EDGE,"E12.0.1.1");Q6=makeQuery(id+"F0.imprint","IMPRINT",FACE,{"disambiguationData":[TD([[makeQuery(id+"F0.imprint","IMPRINT",EDGE,{"derivedFrom":subQ7}),1.0]])]});}
            var Q7;
            {var subQ7=sQuery(id+"F0.wireOp",EDGE,"E12.0.2.1");Q7=makeQuery(id+"F0.imprint","IMPRINT",FACE,{"disambiguationData":[TD([[makeQuery(id+"F0.imprint","IMPRINT",EDGE,{"derivedFrom":subQ7}),1.0]])]});}
            var Q8;
            {var subQ1=sQuery(id+"F0.wireOp",EDGE,"E12.0.3.1");Q8=makeQuery(id+"F0.imprint","IMPRINT",FACE,{"disambiguationData":[TD([[makeQuery(id+"F0.imprint","IMPRINT",EDGE,{"derivedFrom":subQ1}),1.0]])]});}
            extrude(context, id + "F1", {"entities" : qUnion([Q0, Q1, Q2, Q3, Q4, Q5, Q6, Q7, Q8]), "depth" : 5 * mm, "offsetDistance" : 25 * mm});
        }
        {
            var Q0;
            Q0=qCreatedBy(makeId("Top.planeOp"),FACE);
            var sketch = newSketch(context, id + "F2", { "sketchPlane" : qUnion([Q0])});
            skLineSegment(sketch, "E76.bottom", {"start": v(55.45, -66.84) * mm, "end": v(-55.45, -66.84) * mm});
            skLineSegment(sketch, "E76.top", {"start": v(55.45, 66.84) * mm, "end": v(-55.45, 66.84) * mm});
            skLineSegment(sketch, "E76.left", {"start": v(55.45, -66.84) * mm, "end": v(55.45, 66.84) * mm});
            skLineSegment(sketch, "E76.right", {"start": v(-55.45, -66.84) * mm, "end": v(-55.45, 66.84) * mm});
            skPoint(sketch, "E76.middle", {"position": v(0, 0) * mm});
            skSolve(sketch);
        }
        {
            var Q0;
            Q0=makeQuery(id+"F2.imprint","IMPRINT",FACE,{"disambiguationData":[TD([[makeQuery(id+"F2.imprint","IMPRINT",EDGE,{"derivedFrom":sQuery(id+"F2.wireOp",EDGE,"E76.bottom")}),-1.0]])]});
            extrude(context, id + "F3", {"entities" : qUnion([Q0]), "oppositeDirection" : true, "depth" : 5 * mm, "offsetDistance" : 25 * mm});
        }
    });
